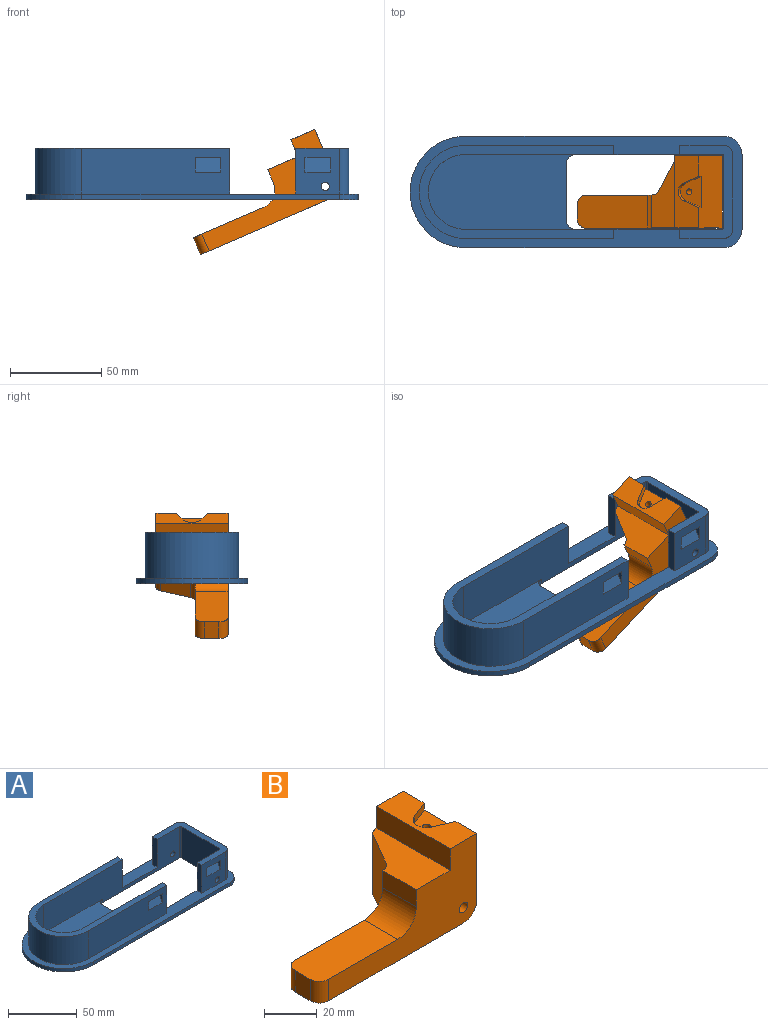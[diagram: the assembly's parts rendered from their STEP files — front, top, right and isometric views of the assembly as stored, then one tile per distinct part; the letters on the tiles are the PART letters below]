
ASSEMBLY  parts=2 mates=1
PART A: 50 faces, bbox 181.5x61x28 mm
  f0: plane 14x4mm, normal (0,0,-1), area 56mm2, adj f1,f2,f3,f13
  f1: plane 14x8mm, normal (0,-0.89,0.45), area 125.2mm2, adj f0,f2,f3,f13
  f2: plane 8x4mm, normal (-1,0,0), area 16mm2, adj f0,f1,f13
  f3: plane 8x4mm, normal (1,0,0), area 16mm2, adj f0,f1,f13
  f4: plane 14x4mm, normal (0,0,-1), area 56mm2, adj f5,f6,f7,f14
  f5: plane 14x8mm, normal (0,0.89,0.45), area 125.2mm2, adj f4,f6,f7,f14
  f6: plane 8x4mm, normal (-1,0,0), area 16mm2, adj f4,f5,f14
  f7: plane 8x4mm, normal (1,0,0), area 16mm2, adj f4,f5,f14
  f8: plane 25x24mm, normal (0,1,0), area 472.1mm2, adj f15,f18,f32,f34,f38,f42,f43,f44
  f9: plane 106.5x51mm, normal (0,0,1), area 1171.3mm2, adj f13,f14,f16,f17,f31,f37,f39,f41
  f10: cylinder r=5mm len=5mm, axis (0,0,-1), area 23.6mm2, adj f12,f16,f28,f40
  f11: cylinder r=5mm len=5mm, axis (0,0,-1), area 23.6mm2, adj f12,f17,f28,f40
  f12: plane 31x3mm, normal (1,0,0), area 93mm2, adj f10,f11,f28,f40
  f13: plane 81x25mm, normal (0,-1,0), area 1913mm2, adj f0,f1,f2,f3,f9,f18,f31,f37
  f14: plane 81x25mm, normal (0,1,0), area 1913mm2, adj f4,f5,f6,f7,f9,f18,f31,f39
  f15: plane 51x29mm, normal (0,0,1), area 484.7mm2, adj f8,f16,f17,f24,f25,f26,f29,f30
  f16: plane 140x28mm, normal (0,-1,0), area 2824.1mm2, adj f9,f10,f15,f18,f24,f28,f34,f38
  f17: plane 140x28mm, normal (0,1,0), area 2824.1mm2, adj f9,f11,f15,f18,f26,f28,f35,f36
  f18: plane 181.5x61mm, normal (0,0,1), area 2532.6mm2, adj f8,f13,f14,f16,f17,f19,f20,f21
  f19: cylinder r=10mm len=10mm, axis (0,0,-1), area 47.1mm2, adj f18,f20,f27,f28
  f20: plane 141x3mm, normal (0,1,0), area 423mm2, adj f18,f19,f21,f28
  f21: cylinder r=30.5mm len=61mm, axis (0,0,-1), area 287.5mm2, adj f18,f20,f22,f28
  f22: plane 141x3mm, normal (0,-1,0), area 423mm2, adj f18,f21,f23,f28
  f23: cylinder r=10mm len=10mm, axis (0,0,-1), area 47.1mm2, adj f18,f22,f27,f28
  f24: cylinder r=1mm len=28mm, axis (0,0,-1), area 44mm2, adj f15,f16,f25,f28
  f25: plane 39x28mm, normal (-1,0,0), area 1092mm2, adj f15,f24,f26,f28
  f26: cylinder r=1mm len=28mm, axis (0,0,-1), area 44mm2, adj f15,f17,f25,f28
  f27: plane 41x3mm, normal (1,0,0), area 123mm2, adj f18,f19,f23,f28
  f28: plane 181.5x61mm, normal (0,0,-1), area 7114.5mm2, adj f10,f11,f12,f16,f17,f19,f20,f21
  f29: cylinder r=5mm len=25mm, axis (0,0,-1), area 196.3mm2, adj f15,f18,f30,f33
  f30: plane 25x24mm, normal (0,-1,0), area 472.1mm2, adj f15,f18,f29,f35,f36,f46,f47,f48
  f31: cylinder r=25.5mm len=51mm, axis (0,0,-1), area 2002.8mm2, adj f9,f13,f14,f18
  f32: cylinder r=5mm len=25mm, axis (0,0,-1), area 196.3mm2, adj f8,f15,f18,f33
  f33: plane 41x25mm, normal (1,0,0), area 1025mm2, adj f15,f18,f29,f32
  f34: cylinder r=2.25mm len=5mm, axis (0,-1,0), area 70.7mm2, adj f8,f16
  f35: cylinder r=2.25mm len=5mm, axis (0,-1,0), area 70.7mm2, adj f17,f30
  f36: plane 25x5mm, normal (-1,0,0), area 125mm2, adj f15,f17,f18,f30
  f37: plane 25x5mm, normal (1,0,0), area 125mm2, adj f9,f13,f17,f18
  f38: plane 25x5mm, normal (-1,0,0), area 125mm2, adj f8,f15,f16,f18
  f39: plane 25x5mm, normal (1,0,0), area 125mm2, adj f9,f14,f16,f18
  f40: plane 80.5x41mm, normal (0,0,1), area 2925.9mm2, adj f10,f11,f12,f16,f17,f41
  f41: cylinder r=20.5mm len=41mm, axis (0,0,1), area 1610.1mm2, adj f9,f16,f17,f40
  f42: plane 14x4mm, normal (0,0,-1), area 56mm2, adj f8,f43,f44,f45
  f43: plane 14x8mm, normal (0,0.89,0.45), area 125.2mm2, adj f8,f42,f44,f45
  f44: plane 8x4mm, normal (1,0,0), area 16mm2, adj f8,f42,f43
  f45: plane 8x4mm, normal (-1,0,0), area 16mm2, adj f8,f42,f43
  f46: plane 14x4mm, normal (0,0,-1), area 56mm2, adj f30,f47,f48,f49
  f47: plane 14x8mm, normal (0,-0.89,0.45), area 125.2mm2, adj f30,f46,f48,f49
  f48: plane 8x4mm, normal (1,0,0), area 16mm2, adj f30,f46,f47
  f49: plane 8x4mm, normal (-1,0,0), area 16mm2, adj f30,f46,f47
PART B: 25 faces, bbox 84.4x39.4x38 mm
  f0: plane 39.4x14.27mm, normal (0,0,1), area 419.4mm2, adj f2,f3,f4,f18,f20,f21,f22
  f1: plane 39.4x18.13mm, normal (0,0,1), area 520.3mm2, adj f4,f10,f11,f12,f14,f18
  f2: plane 39.4x31.62mm, normal (1,0,0), area 1190.4mm2, adj f0,f3,f4,f17,f19,f20,f22
  f3: plane 38x14.27mm, normal (0,1,0), area 515.6mm2, adj f0,f2,f9,f10,f16,f17,f18
  f4: plane 79.4x38mm, normal (0,-1,0), area 1514.7mm2, adj f0,f1,f2,f8,f9,f13,f14,f15
  f5: plane 47x20mm, normal (0,1,0), area 491.5mm2, adj f7,f9,f12,f13,f15
  f6: plane 10x8mm, normal (-1,0,0), area 80mm2, adj f7,f8,f9,f13
  f7: cylinder r=5mm len=10mm, axis (0,0,1), area 78.5mm2, adj f5,f6,f9,f13
  f8: cylinder r=5mm len=10mm, axis (0,0,1), area 78.5mm2, adj f4,f6,f9,f13
  f9: plane 77.26x39.4mm, normal (0,0,-1), area 1726.7mm2, adj f3,f4,f5,f6,f7,f8,f10,f11
  f10: cylinder r=5mm len=28mm, axis (0,0,1), area 146.6mm2, adj f1,f3,f9,f11
  f11: plane 28x16.4mm, normal (-0.87,0.5,0), area 530.2mm2, adj f1,f9,f10,f12
  f12: cylinder r=5mm len=28mm, axis (0,0,1), area 146.6mm2, adj f1,f5,f9,f11,f14
  f13: plane 42x18mm, normal (0,0,1), area 745.3mm2, adj f4,f5,f6,f7,f8,f15
  f14: plane 18x8mm, normal (-1,0,0), area 144mm2, adj f1,f4,f12,f15
  f15: cylinder r=10mm len=18mm, axis (0,-1,0), area 282.7mm2, adj f4,f5,f13,f14
  f16: cylinder r=2.25mm len=39.4mm, axis (0,-1,0), area 557mm2, adj f3,f4
  f17: cylinder r=7.18mm len=39.4mm, axis (0,-1,0), area 412.9mm2, adj f2,f3,f4,f9
  f18: plane 39.4x10mm, normal (-1,0,0), area 394mm2, adj f0,f1,f3,f4
  f19: plane 17.06x12.29mm, normal (0,0,1), area 134.3mm2, adj f2,f20,f21,f22,f24
  f20: plane 9.11x3.77mm, normal (0.38,-0.92,0), area 31.9mm2, adj f0,f2,f19,f21
  f21: cylinder r=5.15mm len=9.52mm, axis (0,0,1), area 39.3mm2, adj f0,f19,f20,f22
  f22: plane 9.11x3.77mm, normal (0.38,0.92,0), area 31.9mm2, adj f0,f2,f19,f21
  f23: plane 3.3x3.3mm, normal (0,0,1), area 8.6mm2, adj f24
  f24: cylinder r=1.65mm len=16.76mm, axis (0,0,1), area 173.9mm2, adj f19,f23
PLACE A at identity fixed
PLACE B rot(axis=(0,-1,0),23.4deg) t=(7.58,0,-22.25)mm
MATE revolute B.f17 <-> A.f34  axis (0,1,0) through (57.56,19.7,7.18)mm
